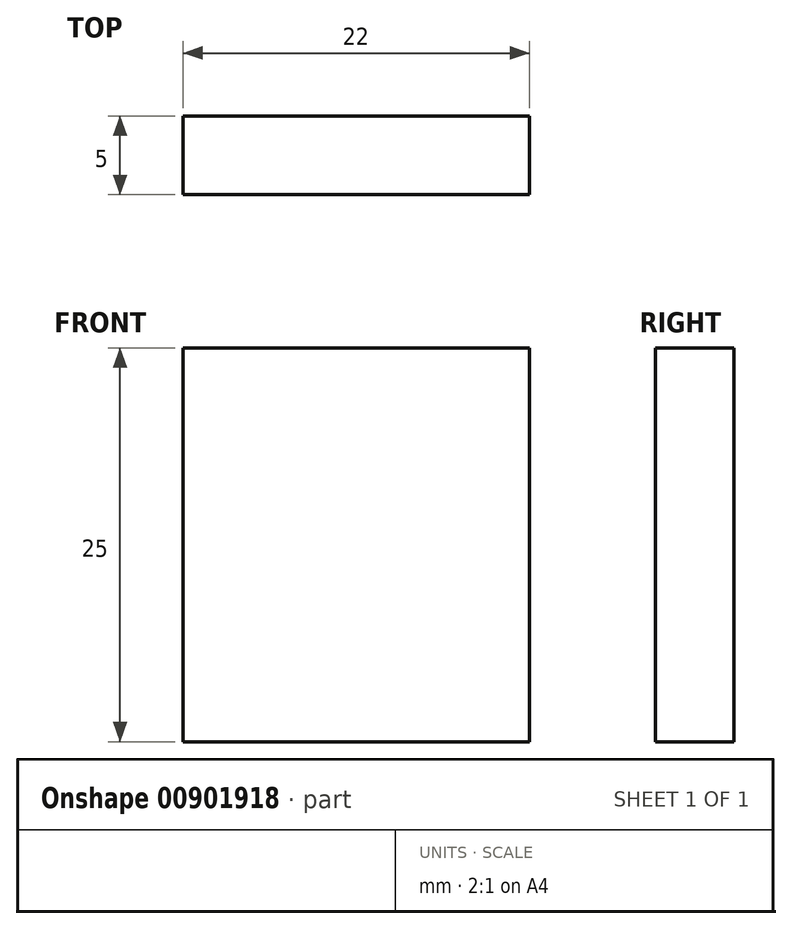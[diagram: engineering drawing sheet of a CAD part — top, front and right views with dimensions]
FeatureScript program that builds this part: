
annotation { "Feature Type Name" : "Feature", "Feature Type Description" : "" }
export const myFeature = defineFeature(function(context is Context, id is Id, definition is map)
    precondition{}
    {
        {
            var Q0;
            Q0=qCreatedBy(makeId("Top.planeOp"),FACE);
            var sketch = newSketch(context, id + "F0", { "sketchPlane" : qUnion([Q0])});
            skLineSegment(sketch, "E0.bottom", {"start": v(-7.9, -15.25) * mm, "end": v(14.1, -15.25) * mm});
            skLineSegment(sketch, "E0.top", {"start": v(-7.9, -20.25) * mm, "end": v(14.1, -20.25) * mm});
            skLineSegment(sketch, "E0.left", {"start": v(-7.9, -15.25) * mm, "end": v(-7.9, -20.25) * mm});
            skLineSegment(sketch, "E0.right", {"start": v(14.1, -15.25) * mm, "end": v(14.1, -20.25) * mm});
            skSolve(sketch);
        }
        {
            var Q0;
            Q0=makeQuery(id+"F0.imprint","IMPRINT",FACE,{"disambiguationData":[TD([[makeQuery(id+"F0.imprint","IMPRINT",EDGE,{"derivedFrom":sQuery(id+"F0.wireOp",EDGE,"E0.bottom")}),-1.0]])]});
            extrude(context, id + "F1", {"entities" : qUnion([Q0]), "depth" : 25 * mm, "offsetDistance" : 25 * mm});
        }
    });
